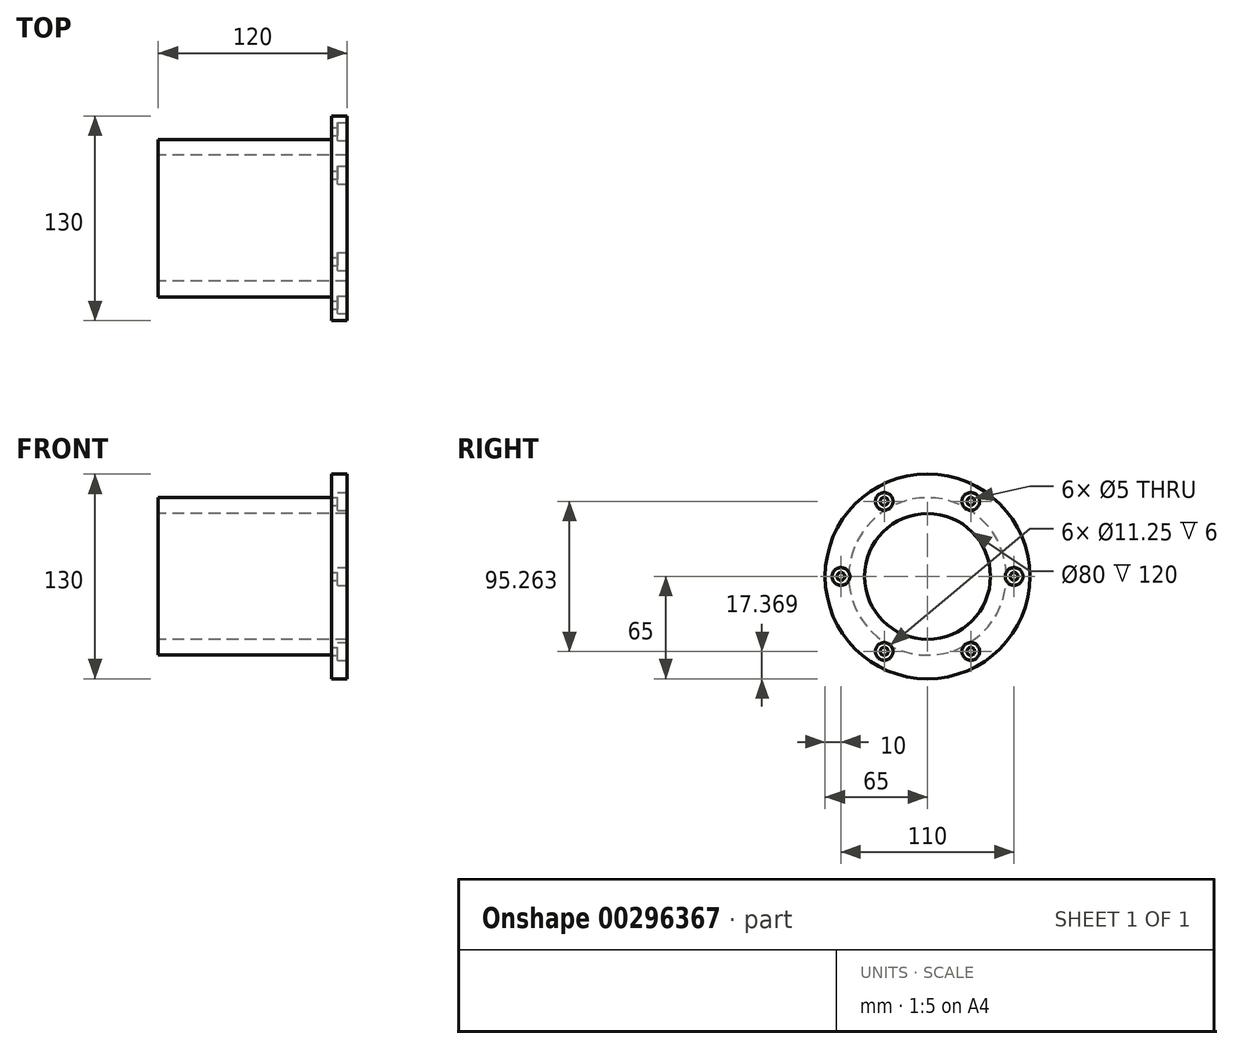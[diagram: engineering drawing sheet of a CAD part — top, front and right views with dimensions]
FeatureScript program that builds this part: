
annotation { "Feature Type Name" : "Feature", "Feature Type Description" : "" }
export const myFeature = defineFeature(function(context is Context, id is Id, definition is map)
    precondition{}
    {
        {
            var Q0;
            Q0=qCreatedBy(makeId("Front.planeOp"),FACE);
            var sketch = newSketch(context, id + "F0", { "sketchPlane" : qUnion([Q0])});
            skLineSegment(sketch, "E0", {"start": v(0, 0) * mm, "end": v(95.43, 0) * mm, "construction": true});
            skLineSegment(sketch, "E1.bottom", {"start": v(0, 40) * mm, "end": v(120, 40) * mm});
            skLineSegment(sketch, "E1.top", {"start": v(0, 50) * mm, "end": v(110, 50) * mm});
            skLineSegment(sketch, "E1.left", {"start": v(0, 40) * mm, "end": v(0, 50) * mm});
            skLineSegment(sketch, "E2.bottom", {"start": v(110, 65) * mm, "end": v(120, 65) * mm});
            skLineSegment(sketch, "E2.left", {"start": v(110, 65) * mm, "end": v(110, 50) * mm});
            skLineSegment(sketch, "E2.right", {"start": v(120, 65) * mm, "end": v(120, 40) * mm});
            skSolve(sketch);
        }
        {
            var Q0;
            Q0=makeQuery(id+"F0.imprint","IMPRINT",FACE,{"disambiguationData":[TD([[makeQuery(id+"F0.imprint","IMPRINT",EDGE,{"derivedFrom":sQuery(id+"F0.wireOp",EDGE,"E1.bottom")}),1.0]])]});
            var Q1;
            Q1=sQuery(id+"F0.wireOp",EDGE,"E0");
            revolve(context, id + "F1", {"entities" : qUnion([Q0]), "axis" : qUnion([Q1]), "revolveType" : RevolveType.FULL});
        }
        {
            var Q0;
            Q0=makeQuery(id+"F1.opRevolve","SWEPT_FACE",FACE,{"disambiguationData":[OSD([sQuery(id+"F0.wireOp",EDGE,"E2.right")])]});
            var sketch = newSketch(context, id + "F2", { "sketchPlane" : qUnion([Q0])});
            skCircle(sketch, "E3.cCircle", {"center": v(0, 0) * mm, "radius": 47.63 * mm, "construction": true});
            skLineSegment(sketch, "E3.0", {"start": v(-27.5, 47.63) * mm, "end": v(27.5, 47.63) * mm, "construction": true});
            skLineSegment(sketch, "E3.1", {"start": v(27.5, 47.63) * mm, "end": v(55, 0) * mm, "construction": true});
            skLineSegment(sketch, "E3.2", {"start": v(55, 0) * mm, "end": v(27.5, -47.63) * mm, "construction": true});
            skLineSegment(sketch, "E3.3", {"start": v(27.5, -47.63) * mm, "end": v(-27.5, -47.63) * mm, "construction": true});
            skLineSegment(sketch, "E3.4", {"start": v(-27.5, -47.63) * mm, "end": v(-55, 0) * mm, "construction": true});
            skLineSegment(sketch, "E3.5", {"start": v(-55, 0) * mm, "end": v(-27.5, 47.63) * mm, "construction": true});
            skPoint(sketch, "E3.0.midPoint", {"position": v(0, 47.63) * mm});
            skPoint(sketch, "E4", {"position": v(-27.5, 47.63) * mm});
            skPoint(sketch, "E5", {"position": v(27.5, 47.63) * mm});
            skPoint(sketch, "E6", {"position": v(55, 0) * mm});
            skPoint(sketch, "E7", {"position": v(27.5, -47.63) * mm});
            skPoint(sketch, "E8", {"position": v(-27.5, -47.63) * mm});
            skPoint(sketch, "E9", {"position": v(-55, 0) * mm});
            skSolve(sketch);
        }
        {
            var Q0;
            Q0=sQuery(id+"F2.wireOp",VERTEX,"E4");
            var Q1;
            Q1=sQuery(id+"F2.wireOp",VERTEX,"E5");
            var Q2;
            Q2=sQuery(id+"F2.wireOp",VERTEX,"E6");
            var Q3;
            Q3=sQuery(id+"F2.wireOp",VERTEX,"E7");
            var Q4;
            Q4=sQuery(id+"F2.wireOp",VERTEX,"E8");
            var Q5;
            Q5=sQuery(id+"F2.wireOp",VERTEX,"E9");
            var Q6;
            Q6=makeQuery(id+"F1.opRevolve","SWEPT_BODY",BODY,{"disambiguationData":[OSD([sQuery(id+"F0.wireOp",EDGE,"E1.bottom"),sQuery(id+"F0.wireOp",EDGE,"E1.top"),sQuery(id+"F0.wireOp",EDGE,"E1.left"),sQuery(id+"F0.wireOp",EDGE,"E2.bottom"),sQuery(id+"F0.wireOp",EDGE,"E2.left"),sQuery(id+"F0.wireOp",EDGE,"E2.right")])]});
            hole(context, id + "F3", {"style" : HoleStyle.C_BORE, "endStyle" : HoleEndStyle.THROUGH, "standardTappedOrClearance" : lookupTablePath({ "standard" : "ISO", "engagement" : "75%", "pitch" : "1 mm", "size" : "M6", "type" : "Tapped" }), "standardBlindInLast" : lookupTablePath({ "standard" : "ISO", "engagement" : "75%", "pitch" : "1 mm", "size" : "M6", "type" : "Tapped" }), "holeDiameter" : 5 * mm, "cBoreDiameter" : 11.25 * mm, "cBoreDepth" : 6 * mm, "showTappedDepth" : true, "tappedDepth" : 9.6 * mm, "tapClearance" : 3, "locations" : qUnion([Q0, Q1, Q2, Q3, Q4, Q5]), "scope" : qUnion([Q6]), "majorDiameter" : 6 * mm});
        }
    });
